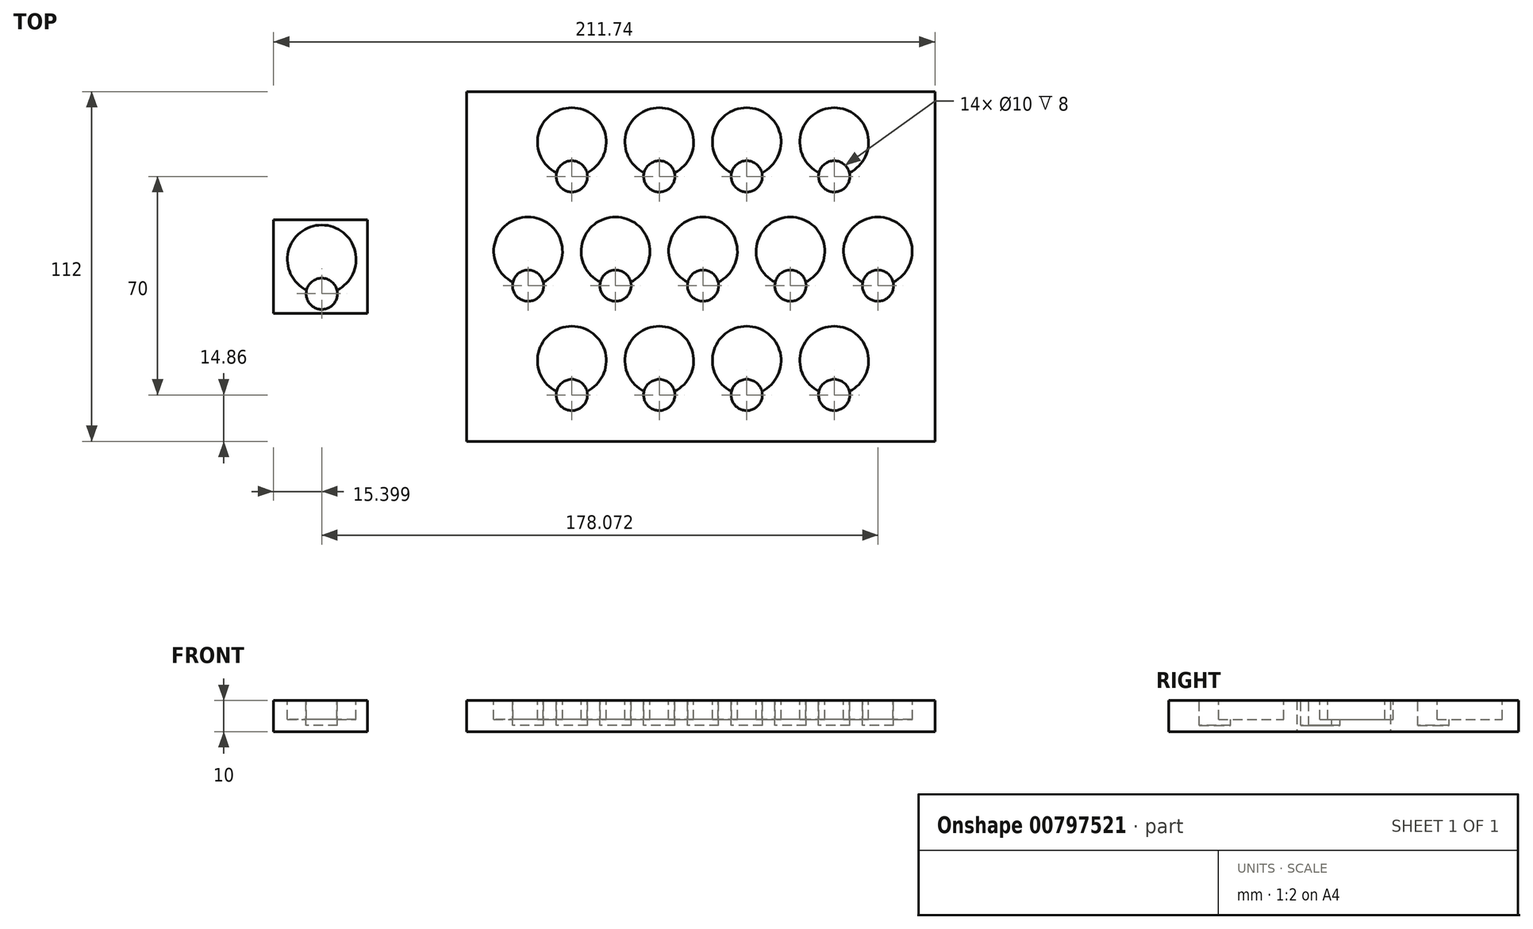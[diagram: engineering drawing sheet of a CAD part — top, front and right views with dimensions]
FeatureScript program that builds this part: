
annotation { "Feature Type Name" : "Feature", "Feature Type Description" : "" }
export const myFeature = defineFeature(function(context is Context, id is Id, definition is map)
    precondition{}
    {
        {
            var Q0;
            Q0=qCreatedBy(makeId("Top.planeOp"),FACE);
            var sketch = newSketch(context, id + "F0", { "sketchPlane" : qUnion([Q0])});
            skLineSegment(sketch, "E0.bottom", {"start": v(-75, 56) * mm, "end": v(75, 56) * mm});
            skLineSegment(sketch, "E0.top", {"start": v(-75, -56) * mm, "end": v(75, -56) * mm});
            skLineSegment(sketch, "E0.left", {"start": v(-75, 56) * mm, "end": v(-75, -56) * mm});
            skLineSegment(sketch, "E0.right", {"start": v(75, 56) * mm, "end": v(75, -56) * mm});
            skPoint(sketch, "E0.middle", {"position": v(0, 0) * mm});
            skLineSegment(sketch, "E1.bottom", {"start": v(-136.74, -15) * mm, "end": v(-106.74, -15) * mm});
            skLineSegment(sketch, "E1.top", {"start": v(-136.74, 15) * mm, "end": v(-106.74, 15) * mm});
            skLineSegment(sketch, "E1.left", {"start": v(-136.74, -15) * mm, "end": v(-136.74, 15) * mm});
            skLineSegment(sketch, "E1.right", {"start": v(-106.74, -15) * mm, "end": v(-106.74, 15) * mm});
            skPoint(sketch, "E1.middle", {"position": v(-121.74, 0) * mm});
            skSolve(sketch);
        }
        {
            var Q0;
            Q0=makeQuery(id+"F0.imprint","IMPRINT",FACE,{"disambiguationData":[TD([[makeQuery(id+"F0.imprint","IMPRINT",EDGE,{"derivedFrom":sQuery(id+"F0.wireOp",EDGE,"E0.bottom")}),-1.0]])]});
            extrude(context, id + "F1", {"entities" : qUnion([Q0]), "depth" : 10 * mm, "offsetDistance" : 25 * mm});
        }
        {
            var Q0;
            Q0=makeQuery(id+"F1.opExtrude","CAP_FACE",FACE,{"disambiguationData":[OSD([sQuery(id+"F0.wireOp",EDGE,"E0.bottom"),sQuery(id+"F0.wireOp",EDGE,"E0.top"),sQuery(id+"F0.wireOp",EDGE,"E0.left"),sQuery(id+"F0.wireOp",EDGE,"E0.right")])],"isStart":false});
            var sketch = newSketch(context, id + "F2", { "sketchPlane" : qUnion([Q0])});
            skCircle(sketch, "E2", {"center": v(-13.27, 39.86) * mm, "radius": 11 * mm});
            skCircle(sketch, "E3", {"center": v(14.73, 39.86) * mm, "radius": 11 * mm});
            skCircle(sketch, "E4", {"center": v(0.73, 4.86) * mm, "radius": 11 * mm});
            skCircle(sketch, "E5", {"center": v(28.73, 4.86) * mm, "radius": 11 * mm});
            skCircle(sketch, "E6", {"center": v(42.73, 39.86) * mm, "radius": 11 * mm});
            skCircle(sketch, "E7", {"center": v(56.73, 4.86) * mm, "radius": 11 * mm});
            skCircle(sketch, "E8", {"center": v(-13.27, -30.14) * mm, "radius": 11 * mm});
            skCircle(sketch, "E9", {"center": v(14.73, -30.14) * mm, "radius": 11 * mm});
            skCircle(sketch, "E10", {"center": v(42.73, -30.14) * mm, "radius": 11 * mm});
            skCircle(sketch, "E11", {"center": v(-27.27, 4.86) * mm, "radius": 11 * mm});
            skCircle(sketch, "E12", {"center": v(-55.27, 4.86) * mm, "radius": 11 * mm});
            skCircle(sketch, "E13", {"center": v(-41.27, 39.86) * mm, "radius": 11 * mm});
            skCircle(sketch, "E14", {"center": v(-41.27, -30.14) * mm, "radius": 11 * mm});
            skLineSegment(sketch, "E15", {"start": v(-41.27, 39.86) * mm, "end": v(-41.27, -30.14) * mm, "construction": true});
            skCircle(sketch, "E16", {"center": v(-13.27, 28.86) * mm, "radius": 5 * mm});
            skCircle(sketch, "E17", {"center": v(14.73, 28.86) * mm, "radius": 5 * mm});
            skCircle(sketch, "E18", {"center": v(42.73, 28.86) * mm, "radius": 5 * mm});
            skCircle(sketch, "E19", {"center": v(-41.27, 28.86) * mm, "radius": 5 * mm});
            skCircle(sketch, "E20", {"center": v(-55.27, -6.14) * mm, "radius": 5 * mm});
            skCircle(sketch, "E21", {"center": v(-27.27, -6.14) * mm, "radius": 5 * mm});
            skCircle(sketch, "E22", {"center": v(0.73, -6.14) * mm, "radius": 5 * mm});
            skCircle(sketch, "E23", {"center": v(28.73, -6.14) * mm, "radius": 5 * mm});
            skCircle(sketch, "E24", {"center": v(56.73, -6.14) * mm, "radius": 5 * mm});
            skCircle(sketch, "E25", {"center": v(-41.27, -41.14) * mm, "radius": 5 * mm});
            skCircle(sketch, "E26", {"center": v(-13.27, -41.14) * mm, "radius": 5 * mm});
            skCircle(sketch, "E27", {"center": v(14.73, -41.14) * mm, "radius": 5 * mm});
            skCircle(sketch, "E28", {"center": v(42.73, -41.14) * mm, "radius": 5 * mm});
            skSolve(sketch);
        }
        {
            var Q0;
            {var subQ0=sQuery(id+"F2.wireOp",EDGE,"E25");var subQ1=sQuery(id+"F2.wireOp",EDGE,"E14");var subQ2=makeQuery(id+"F2.imprint","INTERSECT",VERTEX,{"disambiguationData":[OD(0.0)],"derivedFrom":[subQ1,subQ0]});Q0=makeQuery(id+"F2.imprint","IMPRINT",FACE,{"disambiguationData":[TD([[makeQuery(id+"F2.imprint","IMPRINT",EDGE,{"disambiguationData":[TD([[subQ2,1.0]])],"derivedFrom":subQ1}),1.0]])]});}
            var Q1;
            {var subQ0=sQuery(id+"F2.wireOp",EDGE,"E27");var subQ1=sQuery(id+"F2.wireOp",EDGE,"E9");var subQ2=makeQuery(id+"F2.imprint","INTERSECT",VERTEX,{"disambiguationData":[OD(0.0)],"derivedFrom":[subQ1,subQ0]});Q1=makeQuery(id+"F2.imprint","IMPRINT",FACE,{"disambiguationData":[TD([[makeQuery(id+"F2.imprint","IMPRINT",EDGE,{"disambiguationData":[TD([[subQ2,-1.0]])],"derivedFrom":subQ1}),-1.0]])]});}
            var Q2;
            {var subQ0=sQuery(id+"F2.wireOp",EDGE,"E28");var subQ1=sQuery(id+"F2.wireOp",EDGE,"E10");var subQ2=makeQuery(id+"F2.imprint","INTERSECT",VERTEX,{"disambiguationData":[OD(0.0)],"derivedFrom":[subQ1,subQ0]});Q2=makeQuery(id+"F2.imprint","IMPRINT",FACE,{"disambiguationData":[TD([[makeQuery(id+"F2.imprint","IMPRINT",EDGE,{"disambiguationData":[TD([[subQ2,-1.0]])],"derivedFrom":subQ1}),1.0]])]});}
            var Q3;
            {var subQ0=sQuery(id+"F2.wireOp",EDGE,"E19");var subQ1=sQuery(id+"F2.wireOp",EDGE,"E13");var subQ2=makeQuery(id+"F2.imprint","INTERSECT",VERTEX,{"disambiguationData":[OD(0.0)],"derivedFrom":[subQ1,subQ0]});Q3=makeQuery(id+"F2.imprint","IMPRINT",FACE,{"disambiguationData":[TD([[makeQuery(id+"F2.imprint","IMPRINT",EDGE,{"disambiguationData":[TD([[subQ2,1.0]])],"derivedFrom":subQ1}),1.0]])]});}
            var Q4;
            {var subQ0=sQuery(id+"F2.wireOp",EDGE,"E26");var subQ1=sQuery(id+"F2.wireOp",EDGE,"E8");var subQ2=makeQuery(id+"F2.imprint","INTERSECT",VERTEX,{"disambiguationData":[OD(0.0)],"derivedFrom":[subQ1,subQ0]});Q4=makeQuery(id+"F2.imprint","IMPRINT",FACE,{"disambiguationData":[TD([[makeQuery(id+"F2.imprint","IMPRINT",EDGE,{"disambiguationData":[TD([[subQ2,-1.0]])],"derivedFrom":subQ1}),-1.0]])]});}
            var Q5;
            {var subQ0=sQuery(id+"F2.wireOp",EDGE,"E21");var subQ1=sQuery(id+"F2.wireOp",EDGE,"E11");var subQ2=makeQuery(id+"F2.imprint","INTERSECT",VERTEX,{"disambiguationData":[OD(0.0)],"derivedFrom":[subQ1,subQ0]});Q5=makeQuery(id+"F2.imprint","IMPRINT",FACE,{"disambiguationData":[TD([[makeQuery(id+"F2.imprint","IMPRINT",EDGE,{"disambiguationData":[TD([[subQ2,-1.0]])],"derivedFrom":subQ1}),-1.0]])]});}
            var Q6;
            {var subQ0=sQuery(id+"F2.wireOp",EDGE,"E18");var subQ1=sQuery(id+"F2.wireOp",EDGE,"E6");var subQ2=makeQuery(id+"F2.imprint","INTERSECT",VERTEX,{"disambiguationData":[OD(0.0)],"derivedFrom":[subQ1,subQ0]});Q6=makeQuery(id+"F2.imprint","IMPRINT",FACE,{"disambiguationData":[TD([[makeQuery(id+"F2.imprint","IMPRINT",EDGE,{"disambiguationData":[TD([[subQ2,-1.0]])],"derivedFrom":subQ1}),1.0]])]});}
            var Q7;
            {var subQ0=sQuery(id+"F2.wireOp",EDGE,"E28");var subQ1=sQuery(id+"F2.wireOp",EDGE,"E10");var subQ2=makeQuery(id+"F2.imprint","INTERSECT",VERTEX,{"disambiguationData":[OD(0.0)],"derivedFrom":[subQ1,subQ0]});Q7=makeQuery(id+"F2.imprint","IMPRINT",FACE,{"disambiguationData":[TD([[makeQuery(id+"F2.imprint","IMPRINT",EDGE,{"disambiguationData":[TD([[subQ2,-1.0]])],"derivedFrom":subQ1}),-1.0]])]});}
            var Q8;
            {var subQ0=sQuery(id+"F2.wireOp",EDGE,"E24");var subQ1=sQuery(id+"F2.wireOp",EDGE,"E7");var subQ2=makeQuery(id+"F2.imprint","INTERSECT",VERTEX,{"disambiguationData":[OD(0.0)],"derivedFrom":[subQ1,subQ0]});Q8=makeQuery(id+"F2.imprint","IMPRINT",FACE,{"disambiguationData":[TD([[makeQuery(id+"F2.imprint","IMPRINT",EDGE,{"disambiguationData":[TD([[subQ2,1.0]])],"derivedFrom":subQ1}),1.0]])]});}
            var Q9;
            {var subQ0=sQuery(id+"F2.wireOp",EDGE,"E19");var subQ1=sQuery(id+"F2.wireOp",EDGE,"E13");var subQ2=makeQuery(id+"F2.imprint","INTERSECT",VERTEX,{"disambiguationData":[OD(0.0)],"derivedFrom":[subQ1,subQ0]});Q9=makeQuery(id+"F2.imprint","IMPRINT",FACE,{"disambiguationData":[TD([[makeQuery(id+"F2.imprint","IMPRINT",EDGE,{"disambiguationData":[TD([[subQ2,-1.0]])],"derivedFrom":subQ1}),1.0]])]});}
            var Q10;
            {var subQ0=sQuery(id+"F2.wireOp",EDGE,"E24");var subQ1=sQuery(id+"F2.wireOp",EDGE,"E7");var subQ2=makeQuery(id+"F2.imprint","INTERSECT",VERTEX,{"disambiguationData":[OD(0.0)],"derivedFrom":[subQ1,subQ0]});Q10=makeQuery(id+"F2.imprint","IMPRINT",FACE,{"disambiguationData":[TD([[makeQuery(id+"F2.imprint","IMPRINT",EDGE,{"disambiguationData":[TD([[subQ2,-1.0]])],"derivedFrom":subQ1}),1.0]])]});}
            var Q11;
            {var subQ0=sQuery(id+"F2.wireOp",EDGE,"E27");var subQ1=sQuery(id+"F2.wireOp",EDGE,"E9");var subQ2=makeQuery(id+"F2.imprint","INTERSECT",VERTEX,{"disambiguationData":[OD(0.0)],"derivedFrom":[subQ1,subQ0]});Q11=makeQuery(id+"F2.imprint","IMPRINT",FACE,{"disambiguationData":[TD([[makeQuery(id+"F2.imprint","IMPRINT",EDGE,{"disambiguationData":[TD([[subQ2,-1.0]])],"derivedFrom":subQ1}),1.0]])]});}
            var Q12;
            {var subQ0=sQuery(id+"F2.wireOp",EDGE,"E25");var subQ1=sQuery(id+"F2.wireOp",EDGE,"E14");var subQ2=makeQuery(id+"F2.imprint","INTERSECT",VERTEX,{"disambiguationData":[OD(0.0)],"derivedFrom":[subQ1,subQ0]});Q12=makeQuery(id+"F2.imprint","IMPRINT",FACE,{"disambiguationData":[TD([[makeQuery(id+"F2.imprint","IMPRINT",EDGE,{"disambiguationData":[TD([[subQ2,-1.0]])],"derivedFrom":subQ1}),-1.0]])]});}
            var Q13;
            {var subQ0=sQuery(id+"F2.wireOp",EDGE,"E23");var subQ1=sQuery(id+"F2.wireOp",EDGE,"E5");var subQ2=makeQuery(id+"F2.imprint","INTERSECT",VERTEX,{"disambiguationData":[OD(0.0)],"derivedFrom":[subQ1,subQ0]});Q13=makeQuery(id+"F2.imprint","IMPRINT",FACE,{"disambiguationData":[TD([[makeQuery(id+"F2.imprint","IMPRINT",EDGE,{"disambiguationData":[TD([[subQ2,1.0]])],"derivedFrom":subQ1}),1.0]])]});}
            var Q14;
            {var subQ0=sQuery(id+"F2.wireOp",EDGE,"E26");var subQ1=sQuery(id+"F2.wireOp",EDGE,"E8");var subQ2=makeQuery(id+"F2.imprint","INTERSECT",VERTEX,{"disambiguationData":[OD(0.0)],"derivedFrom":[subQ1,subQ0]});Q14=makeQuery(id+"F2.imprint","IMPRINT",FACE,{"disambiguationData":[TD([[makeQuery(id+"F2.imprint","IMPRINT",EDGE,{"disambiguationData":[TD([[subQ2,-1.0]])],"derivedFrom":subQ1}),1.0]])]});}
            var Q15;
            {var subQ0=sQuery(id+"F2.wireOp",EDGE,"E22");var subQ1=sQuery(id+"F2.wireOp",EDGE,"E4");var subQ2=makeQuery(id+"F2.imprint","INTERSECT",VERTEX,{"disambiguationData":[OD(0.0)],"derivedFrom":[subQ1,subQ0]});Q15=makeQuery(id+"F2.imprint","IMPRINT",FACE,{"disambiguationData":[TD([[makeQuery(id+"F2.imprint","IMPRINT",EDGE,{"disambiguationData":[TD([[subQ2,-1.0]])],"derivedFrom":subQ1}),-1.0]])]});}
            var Q16;
            {var subQ0=sQuery(id+"F2.wireOp",EDGE,"E20");var subQ1=sQuery(id+"F2.wireOp",EDGE,"E12");var subQ2=makeQuery(id+"F2.imprint","INTERSECT",VERTEX,{"disambiguationData":[OD(0.0)],"derivedFrom":[subQ1,subQ0]});Q16=makeQuery(id+"F2.imprint","IMPRINT",FACE,{"disambiguationData":[TD([[makeQuery(id+"F2.imprint","IMPRINT",EDGE,{"disambiguationData":[TD([[subQ2,-1.0]])],"derivedFrom":subQ1}),-1.0]])]});}
            var Q17;
            {var subQ0=sQuery(id+"F2.wireOp",EDGE,"E19");var subQ1=sQuery(id+"F2.wireOp",EDGE,"E13");var subQ2=makeQuery(id+"F2.imprint","INTERSECT",VERTEX,{"disambiguationData":[OD(0.0)],"derivedFrom":[subQ1,subQ0]});Q17=makeQuery(id+"F2.imprint","IMPRINT",FACE,{"disambiguationData":[TD([[makeQuery(id+"F2.imprint","IMPRINT",EDGE,{"disambiguationData":[TD([[subQ2,-1.0]])],"derivedFrom":subQ1}),-1.0]])]});}
            var Q18;
            {var subQ0=sQuery(id+"F2.wireOp",EDGE,"E17");var subQ1=sQuery(id+"F2.wireOp",EDGE,"E3");var subQ2=makeQuery(id+"F2.imprint","INTERSECT",VERTEX,{"disambiguationData":[OD(0.0)],"derivedFrom":[subQ1,subQ0]});Q18=makeQuery(id+"F2.imprint","IMPRINT",FACE,{"disambiguationData":[TD([[makeQuery(id+"F2.imprint","IMPRINT",EDGE,{"disambiguationData":[TD([[subQ2,-1.0]])],"derivedFrom":subQ1}),-1.0]])]});}
            var Q19;
            {var subQ0=sQuery(id+"F2.wireOp",EDGE,"E17");var subQ1=sQuery(id+"F2.wireOp",EDGE,"E3");var subQ2=makeQuery(id+"F2.imprint","INTERSECT",VERTEX,{"disambiguationData":[OD(0.0)],"derivedFrom":[subQ1,subQ0]});Q19=makeQuery(id+"F2.imprint","IMPRINT",FACE,{"disambiguationData":[TD([[makeQuery(id+"F2.imprint","IMPRINT",EDGE,{"disambiguationData":[TD([[subQ2,-1.0]])],"derivedFrom":subQ1}),1.0]])]});}
            var Q20;
            {var subQ0=sQuery(id+"F2.wireOp",EDGE,"E22");var subQ1=sQuery(id+"F2.wireOp",EDGE,"E4");var subQ2=makeQuery(id+"F2.imprint","INTERSECT",VERTEX,{"disambiguationData":[OD(0.0)],"derivedFrom":[subQ1,subQ0]});Q20=makeQuery(id+"F2.imprint","IMPRINT",FACE,{"disambiguationData":[TD([[makeQuery(id+"F2.imprint","IMPRINT",EDGE,{"disambiguationData":[TD([[subQ2,1.0]])],"derivedFrom":subQ1}),1.0]])]});}
            var Q21;
            {var subQ0=sQuery(id+"F2.wireOp",EDGE,"E20");var subQ1=sQuery(id+"F2.wireOp",EDGE,"E12");var subQ2=makeQuery(id+"F2.imprint","INTERSECT",VERTEX,{"disambiguationData":[OD(0.0)],"derivedFrom":[subQ1,subQ0]});Q21=makeQuery(id+"F2.imprint","IMPRINT",FACE,{"disambiguationData":[TD([[makeQuery(id+"F2.imprint","IMPRINT",EDGE,{"disambiguationData":[TD([[subQ2,-1.0]])],"derivedFrom":subQ1}),1.0]])]});}
            var Q22;
            {var subQ0=sQuery(id+"F2.wireOp",EDGE,"E23");var subQ1=sQuery(id+"F2.wireOp",EDGE,"E5");var subQ2=makeQuery(id+"F2.imprint","INTERSECT",VERTEX,{"disambiguationData":[OD(0.0)],"derivedFrom":[subQ1,subQ0]});Q22=makeQuery(id+"F2.imprint","IMPRINT",FACE,{"disambiguationData":[TD([[makeQuery(id+"F2.imprint","IMPRINT",EDGE,{"disambiguationData":[TD([[subQ2,-1.0]])],"derivedFrom":subQ1}),-1.0]])]});}
            var Q23;
            {var subQ0=sQuery(id+"F2.wireOp",EDGE,"E23");var subQ1=sQuery(id+"F2.wireOp",EDGE,"E5");var subQ2=makeQuery(id+"F2.imprint","INTERSECT",VERTEX,{"disambiguationData":[OD(0.0)],"derivedFrom":[subQ1,subQ0]});Q23=makeQuery(id+"F2.imprint","IMPRINT",FACE,{"disambiguationData":[TD([[makeQuery(id+"F2.imprint","IMPRINT",EDGE,{"disambiguationData":[TD([[subQ2,-1.0]])],"derivedFrom":subQ1}),1.0]])]});}
            var Q24;
            {var subQ0=sQuery(id+"F2.wireOp",EDGE,"E17");var subQ1=sQuery(id+"F2.wireOp",EDGE,"E3");var subQ2=makeQuery(id+"F2.imprint","INTERSECT",VERTEX,{"disambiguationData":[OD(0.0)],"derivedFrom":[subQ1,subQ0]});Q24=makeQuery(id+"F2.imprint","IMPRINT",FACE,{"disambiguationData":[TD([[makeQuery(id+"F2.imprint","IMPRINT",EDGE,{"disambiguationData":[TD([[subQ2,1.0]])],"derivedFrom":subQ1}),1.0]])]});}
            var Q25;
            {var subQ0=sQuery(id+"F2.wireOp",EDGE,"E16");var subQ1=sQuery(id+"F2.wireOp",EDGE,"E2");var subQ2=makeQuery(id+"F2.imprint","INTERSECT",VERTEX,{"disambiguationData":[OD(0.0)],"derivedFrom":[subQ1,subQ0]});Q25=makeQuery(id+"F2.imprint","IMPRINT",FACE,{"disambiguationData":[TD([[makeQuery(id+"F2.imprint","IMPRINT",EDGE,{"disambiguationData":[TD([[subQ2,1.0]])],"derivedFrom":subQ1}),1.0]])]});}
            var Q26;
            {var subQ0=sQuery(id+"F2.wireOp",EDGE,"E18");var subQ1=sQuery(id+"F2.wireOp",EDGE,"E6");var subQ2=makeQuery(id+"F2.imprint","INTERSECT",VERTEX,{"disambiguationData":[OD(0.0)],"derivedFrom":[subQ1,subQ0]});Q26=makeQuery(id+"F2.imprint","IMPRINT",FACE,{"disambiguationData":[TD([[makeQuery(id+"F2.imprint","IMPRINT",EDGE,{"disambiguationData":[TD([[subQ2,-1.0]])],"derivedFrom":subQ1}),-1.0]])]});}
            var Q27;
            {var subQ0=sQuery(id+"F2.wireOp",EDGE,"E16");var subQ1=sQuery(id+"F2.wireOp",EDGE,"E2");var subQ2=makeQuery(id+"F2.imprint","INTERSECT",VERTEX,{"disambiguationData":[OD(0.0)],"derivedFrom":[subQ1,subQ0]});Q27=makeQuery(id+"F2.imprint","IMPRINT",FACE,{"disambiguationData":[TD([[makeQuery(id+"F2.imprint","IMPRINT",EDGE,{"disambiguationData":[TD([[subQ2,-1.0]])],"derivedFrom":subQ1}),-1.0]])]});}
            var Q28;
            {var subQ0=sQuery(id+"F2.wireOp",EDGE,"E16");var subQ1=sQuery(id+"F2.wireOp",EDGE,"E2");var subQ2=makeQuery(id+"F2.imprint","INTERSECT",VERTEX,{"disambiguationData":[OD(0.0)],"derivedFrom":[subQ1,subQ0]});Q28=makeQuery(id+"F2.imprint","IMPRINT",FACE,{"disambiguationData":[TD([[makeQuery(id+"F2.imprint","IMPRINT",EDGE,{"disambiguationData":[TD([[subQ2,-1.0]])],"derivedFrom":subQ1}),1.0]])]});}
            var Q29;
            {var subQ0=sQuery(id+"F2.wireOp",EDGE,"E18");var subQ1=sQuery(id+"F2.wireOp",EDGE,"E6");var subQ2=makeQuery(id+"F2.imprint","INTERSECT",VERTEX,{"disambiguationData":[OD(0.0)],"derivedFrom":[subQ1,subQ0]});Q29=makeQuery(id+"F2.imprint","IMPRINT",FACE,{"disambiguationData":[TD([[makeQuery(id+"F2.imprint","IMPRINT",EDGE,{"disambiguationData":[TD([[subQ2,1.0]])],"derivedFrom":subQ1}),1.0]])]});}
            var Q30;
            {var subQ0=sQuery(id+"F2.wireOp",EDGE,"E27");var subQ1=sQuery(id+"F2.wireOp",EDGE,"E9");var subQ2=makeQuery(id+"F2.imprint","INTERSECT",VERTEX,{"disambiguationData":[OD(0.0)],"derivedFrom":[subQ1,subQ0]});Q30=makeQuery(id+"F2.imprint","IMPRINT",FACE,{"disambiguationData":[TD([[makeQuery(id+"F2.imprint","IMPRINT",EDGE,{"disambiguationData":[TD([[subQ2,1.0]])],"derivedFrom":subQ1}),1.0]])]});}
            var Q31;
            {var subQ0=sQuery(id+"F2.wireOp",EDGE,"E28");var subQ1=sQuery(id+"F2.wireOp",EDGE,"E10");var subQ2=makeQuery(id+"F2.imprint","INTERSECT",VERTEX,{"disambiguationData":[OD(0.0)],"derivedFrom":[subQ1,subQ0]});Q31=makeQuery(id+"F2.imprint","IMPRINT",FACE,{"disambiguationData":[TD([[makeQuery(id+"F2.imprint","IMPRINT",EDGE,{"disambiguationData":[TD([[subQ2,1.0]])],"derivedFrom":subQ1}),1.0]])]});}
            var Q32;
            {var subQ0=sQuery(id+"F2.wireOp",EDGE,"E21");var subQ1=sQuery(id+"F2.wireOp",EDGE,"E11");var subQ2=makeQuery(id+"F2.imprint","INTERSECT",VERTEX,{"disambiguationData":[OD(0.0)],"derivedFrom":[subQ1,subQ0]});Q32=makeQuery(id+"F2.imprint","IMPRINT",FACE,{"disambiguationData":[TD([[makeQuery(id+"F2.imprint","IMPRINT",EDGE,{"disambiguationData":[TD([[subQ2,1.0]])],"derivedFrom":subQ1}),1.0]])]});}
            var Q33;
            {var subQ0=sQuery(id+"F2.wireOp",EDGE,"E25");var subQ1=sQuery(id+"F2.wireOp",EDGE,"E14");var subQ2=makeQuery(id+"F2.imprint","INTERSECT",VERTEX,{"disambiguationData":[OD(0.0)],"derivedFrom":[subQ1,subQ0]});Q33=makeQuery(id+"F2.imprint","IMPRINT",FACE,{"disambiguationData":[TD([[makeQuery(id+"F2.imprint","IMPRINT",EDGE,{"disambiguationData":[TD([[subQ2,-1.0]])],"derivedFrom":subQ1}),1.0]])]});}
            var Q34;
            {var subQ0=sQuery(id+"F2.wireOp",EDGE,"E21");var subQ1=sQuery(id+"F2.wireOp",EDGE,"E11");var subQ2=makeQuery(id+"F2.imprint","INTERSECT",VERTEX,{"disambiguationData":[OD(0.0)],"derivedFrom":[subQ1,subQ0]});Q34=makeQuery(id+"F2.imprint","IMPRINT",FACE,{"disambiguationData":[TD([[makeQuery(id+"F2.imprint","IMPRINT",EDGE,{"disambiguationData":[TD([[subQ2,-1.0]])],"derivedFrom":subQ1}),1.0]])]});}
            var Q35;
            {var subQ0=sQuery(id+"F2.wireOp",EDGE,"E26");var subQ1=sQuery(id+"F2.wireOp",EDGE,"E8");var subQ2=makeQuery(id+"F2.imprint","INTERSECT",VERTEX,{"disambiguationData":[OD(0.0)],"derivedFrom":[subQ1,subQ0]});Q35=makeQuery(id+"F2.imprint","IMPRINT",FACE,{"disambiguationData":[TD([[makeQuery(id+"F2.imprint","IMPRINT",EDGE,{"disambiguationData":[TD([[subQ2,1.0]])],"derivedFrom":subQ1}),1.0]])]});}
            var Q36;
            {var subQ0=sQuery(id+"F2.wireOp",EDGE,"E20");var subQ1=sQuery(id+"F2.wireOp",EDGE,"E12");var subQ2=makeQuery(id+"F2.imprint","INTERSECT",VERTEX,{"disambiguationData":[OD(0.0)],"derivedFrom":[subQ1,subQ0]});Q36=makeQuery(id+"F2.imprint","IMPRINT",FACE,{"disambiguationData":[TD([[makeQuery(id+"F2.imprint","IMPRINT",EDGE,{"disambiguationData":[TD([[subQ2,1.0]])],"derivedFrom":subQ1}),1.0]])]});}
            var Q37;
            {var subQ0=sQuery(id+"F2.wireOp",EDGE,"E24");var subQ1=sQuery(id+"F2.wireOp",EDGE,"E7");var subQ2=makeQuery(id+"F2.imprint","INTERSECT",VERTEX,{"disambiguationData":[OD(0.0)],"derivedFrom":[subQ1,subQ0]});Q37=makeQuery(id+"F2.imprint","IMPRINT",FACE,{"disambiguationData":[TD([[makeQuery(id+"F2.imprint","IMPRINT",EDGE,{"disambiguationData":[TD([[subQ2,-1.0]])],"derivedFrom":subQ1}),-1.0]])]});}
            var Q38;
            {var subQ0=sQuery(id+"F2.wireOp",EDGE,"E22");var subQ1=sQuery(id+"F2.wireOp",EDGE,"E4");var subQ2=makeQuery(id+"F2.imprint","INTERSECT",VERTEX,{"disambiguationData":[OD(0.0)],"derivedFrom":[subQ1,subQ0]});Q38=makeQuery(id+"F2.imprint","IMPRINT",FACE,{"disambiguationData":[TD([[makeQuery(id+"F2.imprint","IMPRINT",EDGE,{"disambiguationData":[TD([[subQ2,-1.0]])],"derivedFrom":subQ1}),1.0]])]});}
            extrude(context, id + "F3", {"entities" : qUnion([Q0, Q1, Q2, Q3, Q4, Q5, Q6, Q7, Q8, Q9, Q10, Q11, Q12, Q13, Q14, Q15, Q16, Q17, Q18, Q19, Q20, Q21, Q22, Q23, Q24, Q25, Q26, Q27, Q28, Q29, Q30, Q31, Q32, Q33, Q34, Q35, Q36, Q37, Q38]), "operationType" : NewBodyOperationType.REMOVE, "oppositeDirection" : true, "depth" : 6 * mm, "offsetDistance" : 25 * mm});
        }
        {
            var Q0;
            {var subQ0=sQuery(id+"F2.wireOp",EDGE,"E19");var subQ1=sQuery(id+"F2.wireOp",EDGE,"E13");var subQ2=makeQuery(id+"F2.imprint","INTERSECT",VERTEX,{"disambiguationData":[OD(0.0)],"derivedFrom":[subQ1,subQ0]});Q0=makeQuery(id+"F2.imprint","IMPRINT",FACE,{"disambiguationData":[TD([[makeQuery(id+"F2.imprint","IMPRINT",EDGE,{"disambiguationData":[TD([[subQ2,-1.0]])],"derivedFrom":subQ1}),1.0]])]});}
            var Q1;
            {var subQ0=sQuery(id+"F2.wireOp",EDGE,"E19");var subQ1=sQuery(id+"F2.wireOp",EDGE,"E13");var subQ2=makeQuery(id+"F2.imprint","INTERSECT",VERTEX,{"disambiguationData":[OD(0.0)],"derivedFrom":[subQ1,subQ0]});Q1=makeQuery(id+"F2.imprint","IMPRINT",FACE,{"disambiguationData":[TD([[makeQuery(id+"F2.imprint","IMPRINT",EDGE,{"disambiguationData":[TD([[subQ2,-1.0]])],"derivedFrom":subQ1}),-1.0]])]});}
            var Q2;
            {var subQ0=sQuery(id+"F2.wireOp",EDGE,"E16");var subQ1=sQuery(id+"F2.wireOp",EDGE,"E2");var subQ2=makeQuery(id+"F2.imprint","INTERSECT",VERTEX,{"disambiguationData":[OD(0.0)],"derivedFrom":[subQ1,subQ0]});Q2=makeQuery(id+"F2.imprint","IMPRINT",FACE,{"disambiguationData":[TD([[makeQuery(id+"F2.imprint","IMPRINT",EDGE,{"disambiguationData":[TD([[subQ2,-1.0]])],"derivedFrom":subQ1}),1.0]])]});}
            var Q3;
            {var subQ0=sQuery(id+"F2.wireOp",EDGE,"E16");var subQ1=sQuery(id+"F2.wireOp",EDGE,"E2");var subQ2=makeQuery(id+"F2.imprint","INTERSECT",VERTEX,{"disambiguationData":[OD(0.0)],"derivedFrom":[subQ1,subQ0]});Q3=makeQuery(id+"F2.imprint","IMPRINT",FACE,{"disambiguationData":[TD([[makeQuery(id+"F2.imprint","IMPRINT",EDGE,{"disambiguationData":[TD([[subQ2,-1.0]])],"derivedFrom":subQ1}),-1.0]])]});}
            var Q4;
            {var subQ0=sQuery(id+"F2.wireOp",EDGE,"E17");var subQ1=sQuery(id+"F2.wireOp",EDGE,"E3");var subQ2=makeQuery(id+"F2.imprint","INTERSECT",VERTEX,{"disambiguationData":[OD(0.0)],"derivedFrom":[subQ1,subQ0]});Q4=makeQuery(id+"F2.imprint","IMPRINT",FACE,{"disambiguationData":[TD([[makeQuery(id+"F2.imprint","IMPRINT",EDGE,{"disambiguationData":[TD([[subQ2,-1.0]])],"derivedFrom":subQ1}),1.0]])]});}
            var Q5;
            {var subQ0=sQuery(id+"F2.wireOp",EDGE,"E17");var subQ1=sQuery(id+"F2.wireOp",EDGE,"E3");var subQ2=makeQuery(id+"F2.imprint","INTERSECT",VERTEX,{"disambiguationData":[OD(0.0)],"derivedFrom":[subQ1,subQ0]});Q5=makeQuery(id+"F2.imprint","IMPRINT",FACE,{"disambiguationData":[TD([[makeQuery(id+"F2.imprint","IMPRINT",EDGE,{"disambiguationData":[TD([[subQ2,-1.0]])],"derivedFrom":subQ1}),-1.0]])]});}
            var Q6;
            {var subQ0=sQuery(id+"F2.wireOp",EDGE,"E18");var subQ1=sQuery(id+"F2.wireOp",EDGE,"E6");var subQ2=makeQuery(id+"F2.imprint","INTERSECT",VERTEX,{"disambiguationData":[OD(0.0)],"derivedFrom":[subQ1,subQ0]});Q6=makeQuery(id+"F2.imprint","IMPRINT",FACE,{"disambiguationData":[TD([[makeQuery(id+"F2.imprint","IMPRINT",EDGE,{"disambiguationData":[TD([[subQ2,-1.0]])],"derivedFrom":subQ1}),1.0]])]});}
            var Q7;
            {var subQ0=sQuery(id+"F2.wireOp",EDGE,"E18");var subQ1=sQuery(id+"F2.wireOp",EDGE,"E6");var subQ2=makeQuery(id+"F2.imprint","INTERSECT",VERTEX,{"disambiguationData":[OD(0.0)],"derivedFrom":[subQ1,subQ0]});Q7=makeQuery(id+"F2.imprint","IMPRINT",FACE,{"disambiguationData":[TD([[makeQuery(id+"F2.imprint","IMPRINT",EDGE,{"disambiguationData":[TD([[subQ2,-1.0]])],"derivedFrom":subQ1}),-1.0]])]});}
            var Q8;
            {var subQ0=sQuery(id+"F2.wireOp",EDGE,"E20");var subQ1=sQuery(id+"F2.wireOp",EDGE,"E12");var subQ2=makeQuery(id+"F2.imprint","INTERSECT",VERTEX,{"disambiguationData":[OD(0.0)],"derivedFrom":[subQ1,subQ0]});Q8=makeQuery(id+"F2.imprint","IMPRINT",FACE,{"disambiguationData":[TD([[makeQuery(id+"F2.imprint","IMPRINT",EDGE,{"disambiguationData":[TD([[subQ2,-1.0]])],"derivedFrom":subQ1}),1.0]])]});}
            var Q9;
            {var subQ0=sQuery(id+"F2.wireOp",EDGE,"E20");var subQ1=sQuery(id+"F2.wireOp",EDGE,"E12");var subQ2=makeQuery(id+"F2.imprint","INTERSECT",VERTEX,{"disambiguationData":[OD(0.0)],"derivedFrom":[subQ1,subQ0]});Q9=makeQuery(id+"F2.imprint","IMPRINT",FACE,{"disambiguationData":[TD([[makeQuery(id+"F2.imprint","IMPRINT",EDGE,{"disambiguationData":[TD([[subQ2,-1.0]])],"derivedFrom":subQ1}),-1.0]])]});}
            var Q10;
            {var subQ0=sQuery(id+"F2.wireOp",EDGE,"E21");var subQ1=sQuery(id+"F2.wireOp",EDGE,"E11");var subQ2=makeQuery(id+"F2.imprint","INTERSECT",VERTEX,{"disambiguationData":[OD(0.0)],"derivedFrom":[subQ1,subQ0]});Q10=makeQuery(id+"F2.imprint","IMPRINT",FACE,{"disambiguationData":[TD([[makeQuery(id+"F2.imprint","IMPRINT",EDGE,{"disambiguationData":[TD([[subQ2,-1.0]])],"derivedFrom":subQ1}),1.0]])]});}
            var Q11;
            {var subQ0=sQuery(id+"F2.wireOp",EDGE,"E21");var subQ1=sQuery(id+"F2.wireOp",EDGE,"E11");var subQ2=makeQuery(id+"F2.imprint","INTERSECT",VERTEX,{"disambiguationData":[OD(0.0)],"derivedFrom":[subQ1,subQ0]});Q11=makeQuery(id+"F2.imprint","IMPRINT",FACE,{"disambiguationData":[TD([[makeQuery(id+"F2.imprint","IMPRINT",EDGE,{"disambiguationData":[TD([[subQ2,-1.0]])],"derivedFrom":subQ1}),-1.0]])]});}
            var Q12;
            {var subQ0=sQuery(id+"F2.wireOp",EDGE,"E22");var subQ1=sQuery(id+"F2.wireOp",EDGE,"E4");var subQ2=makeQuery(id+"F2.imprint","INTERSECT",VERTEX,{"disambiguationData":[OD(0.0)],"derivedFrom":[subQ1,subQ0]});Q12=makeQuery(id+"F2.imprint","IMPRINT",FACE,{"disambiguationData":[TD([[makeQuery(id+"F2.imprint","IMPRINT",EDGE,{"disambiguationData":[TD([[subQ2,-1.0]])],"derivedFrom":subQ1}),1.0]])]});}
            var Q13;
            {var subQ0=sQuery(id+"F2.wireOp",EDGE,"E22");var subQ1=sQuery(id+"F2.wireOp",EDGE,"E4");var subQ2=makeQuery(id+"F2.imprint","INTERSECT",VERTEX,{"disambiguationData":[OD(0.0)],"derivedFrom":[subQ1,subQ0]});Q13=makeQuery(id+"F2.imprint","IMPRINT",FACE,{"disambiguationData":[TD([[makeQuery(id+"F2.imprint","IMPRINT",EDGE,{"disambiguationData":[TD([[subQ2,-1.0]])],"derivedFrom":subQ1}),-1.0]])]});}
            var Q14;
            {var subQ0=sQuery(id+"F2.wireOp",EDGE,"E23");var subQ1=sQuery(id+"F2.wireOp",EDGE,"E5");var subQ2=makeQuery(id+"F2.imprint","INTERSECT",VERTEX,{"disambiguationData":[OD(0.0)],"derivedFrom":[subQ1,subQ0]});Q14=makeQuery(id+"F2.imprint","IMPRINT",FACE,{"disambiguationData":[TD([[makeQuery(id+"F2.imprint","IMPRINT",EDGE,{"disambiguationData":[TD([[subQ2,-1.0]])],"derivedFrom":subQ1}),1.0]])]});}
            var Q15;
            {var subQ0=sQuery(id+"F2.wireOp",EDGE,"E23");var subQ1=sQuery(id+"F2.wireOp",EDGE,"E5");var subQ2=makeQuery(id+"F2.imprint","INTERSECT",VERTEX,{"disambiguationData":[OD(0.0)],"derivedFrom":[subQ1,subQ0]});Q15=makeQuery(id+"F2.imprint","IMPRINT",FACE,{"disambiguationData":[TD([[makeQuery(id+"F2.imprint","IMPRINT",EDGE,{"disambiguationData":[TD([[subQ2,-1.0]])],"derivedFrom":subQ1}),-1.0]])]});}
            var Q16;
            {var subQ0=sQuery(id+"F2.wireOp",EDGE,"E24");var subQ1=sQuery(id+"F2.wireOp",EDGE,"E7");var subQ2=makeQuery(id+"F2.imprint","INTERSECT",VERTEX,{"disambiguationData":[OD(0.0)],"derivedFrom":[subQ1,subQ0]});Q16=makeQuery(id+"F2.imprint","IMPRINT",FACE,{"disambiguationData":[TD([[makeQuery(id+"F2.imprint","IMPRINT",EDGE,{"disambiguationData":[TD([[subQ2,-1.0]])],"derivedFrom":subQ1}),1.0]])]});}
            var Q17;
            {var subQ0=sQuery(id+"F2.wireOp",EDGE,"E24");var subQ1=sQuery(id+"F2.wireOp",EDGE,"E7");var subQ2=makeQuery(id+"F2.imprint","INTERSECT",VERTEX,{"disambiguationData":[OD(0.0)],"derivedFrom":[subQ1,subQ0]});Q17=makeQuery(id+"F2.imprint","IMPRINT",FACE,{"disambiguationData":[TD([[makeQuery(id+"F2.imprint","IMPRINT",EDGE,{"disambiguationData":[TD([[subQ2,-1.0]])],"derivedFrom":subQ1}),-1.0]])]});}
            var Q18;
            {var subQ0=sQuery(id+"F2.wireOp",EDGE,"E25");var subQ1=sQuery(id+"F2.wireOp",EDGE,"E14");var subQ2=makeQuery(id+"F2.imprint","INTERSECT",VERTEX,{"disambiguationData":[OD(0.0)],"derivedFrom":[subQ1,subQ0]});Q18=makeQuery(id+"F2.imprint","IMPRINT",FACE,{"disambiguationData":[TD([[makeQuery(id+"F2.imprint","IMPRINT",EDGE,{"disambiguationData":[TD([[subQ2,-1.0]])],"derivedFrom":subQ1}),1.0]])]});}
            var Q19;
            {var subQ0=sQuery(id+"F2.wireOp",EDGE,"E25");var subQ1=sQuery(id+"F2.wireOp",EDGE,"E14");var subQ2=makeQuery(id+"F2.imprint","INTERSECT",VERTEX,{"disambiguationData":[OD(0.0)],"derivedFrom":[subQ1,subQ0]});Q19=makeQuery(id+"F2.imprint","IMPRINT",FACE,{"disambiguationData":[TD([[makeQuery(id+"F2.imprint","IMPRINT",EDGE,{"disambiguationData":[TD([[subQ2,-1.0]])],"derivedFrom":subQ1}),-1.0]])]});}
            var Q20;
            {var subQ0=sQuery(id+"F2.wireOp",EDGE,"E26");var subQ1=sQuery(id+"F2.wireOp",EDGE,"E8");var subQ2=makeQuery(id+"F2.imprint","INTERSECT",VERTEX,{"disambiguationData":[OD(0.0)],"derivedFrom":[subQ1,subQ0]});Q20=makeQuery(id+"F2.imprint","IMPRINT",FACE,{"disambiguationData":[TD([[makeQuery(id+"F2.imprint","IMPRINT",EDGE,{"disambiguationData":[TD([[subQ2,-1.0]])],"derivedFrom":subQ1}),1.0]])]});}
            var Q21;
            {var subQ0=sQuery(id+"F2.wireOp",EDGE,"E26");var subQ1=sQuery(id+"F2.wireOp",EDGE,"E8");var subQ2=makeQuery(id+"F2.imprint","INTERSECT",VERTEX,{"disambiguationData":[OD(0.0)],"derivedFrom":[subQ1,subQ0]});Q21=makeQuery(id+"F2.imprint","IMPRINT",FACE,{"disambiguationData":[TD([[makeQuery(id+"F2.imprint","IMPRINT",EDGE,{"disambiguationData":[TD([[subQ2,-1.0]])],"derivedFrom":subQ1}),-1.0]])]});}
            var Q22;
            {var subQ0=sQuery(id+"F2.wireOp",EDGE,"E27");var subQ1=sQuery(id+"F2.wireOp",EDGE,"E9");var subQ2=makeQuery(id+"F2.imprint","INTERSECT",VERTEX,{"disambiguationData":[OD(0.0)],"derivedFrom":[subQ1,subQ0]});Q22=makeQuery(id+"F2.imprint","IMPRINT",FACE,{"disambiguationData":[TD([[makeQuery(id+"F2.imprint","IMPRINT",EDGE,{"disambiguationData":[TD([[subQ2,-1.0]])],"derivedFrom":subQ1}),1.0]])]});}
            var Q23;
            {var subQ0=sQuery(id+"F2.wireOp",EDGE,"E27");var subQ1=sQuery(id+"F2.wireOp",EDGE,"E9");var subQ2=makeQuery(id+"F2.imprint","INTERSECT",VERTEX,{"disambiguationData":[OD(0.0)],"derivedFrom":[subQ1,subQ0]});Q23=makeQuery(id+"F2.imprint","IMPRINT",FACE,{"disambiguationData":[TD([[makeQuery(id+"F2.imprint","IMPRINT",EDGE,{"disambiguationData":[TD([[subQ2,-1.0]])],"derivedFrom":subQ1}),-1.0]])]});}
            var Q24;
            {var subQ0=sQuery(id+"F2.wireOp",EDGE,"E28");var subQ1=sQuery(id+"F2.wireOp",EDGE,"E10");var subQ2=makeQuery(id+"F2.imprint","INTERSECT",VERTEX,{"disambiguationData":[OD(0.0)],"derivedFrom":[subQ1,subQ0]});Q24=makeQuery(id+"F2.imprint","IMPRINT",FACE,{"disambiguationData":[TD([[makeQuery(id+"F2.imprint","IMPRINT",EDGE,{"disambiguationData":[TD([[subQ2,-1.0]])],"derivedFrom":subQ1}),1.0]])]});}
            var Q25;
            {var subQ0=sQuery(id+"F2.wireOp",EDGE,"E28");var subQ1=sQuery(id+"F2.wireOp",EDGE,"E10");var subQ2=makeQuery(id+"F2.imprint","INTERSECT",VERTEX,{"disambiguationData":[OD(0.0)],"derivedFrom":[subQ1,subQ0]});Q25=makeQuery(id+"F2.imprint","IMPRINT",FACE,{"disambiguationData":[TD([[makeQuery(id+"F2.imprint","IMPRINT",EDGE,{"disambiguationData":[TD([[subQ2,-1.0]])],"derivedFrom":subQ1}),-1.0]])]});}
            extrude(context, id + "F4", {"entities" : qUnion([Q0, Q1, Q2, Q3, Q4, Q5, Q6, Q7, Q8, Q9, Q10, Q11, Q12, Q13, Q14, Q15, Q16, Q17, Q18, Q19, Q20, Q21, Q22, Q23, Q24, Q25]), "operationType" : NewBodyOperationType.REMOVE, "oppositeDirection" : true, "depth" : 8 * mm, "offsetDistance" : 25 * mm});
        }
        {
            var Q0;
            Q0=makeQuery(id+"F0.imprint","IMPRINT",FACE,{"disambiguationData":[TD([[makeQuery(id+"F0.imprint","IMPRINT",EDGE,{"derivedFrom":sQuery(id+"F0.wireOp",EDGE,"E1.bottom")}),1.0]])]});
            extrude(context, id + "F5", {"entities" : qUnion([Q0]), "depth" : 10 * mm, "offsetDistance" : 25 * mm});
        }
        {
            var Q0;
            Q0=makeQuery(id+"F5.opExtrude","CAP_FACE",FACE,{"disambiguationData":[OSD([sQuery(id+"F0.wireOp",EDGE,"E1.bottom"),sQuery(id+"F0.wireOp",EDGE,"E1.top"),sQuery(id+"F0.wireOp",EDGE,"E1.left"),sQuery(id+"F0.wireOp",EDGE,"E1.right")])],"isStart":false});
            var sketch = newSketch(context, id + "F6", { "sketchPlane" : qUnion([Q0])});
            skCircle(sketch, "E29", {"center": v(-121.34, 2.28) * mm, "radius": 11 * mm});
            skCircle(sketch, "E30", {"center": v(-121.34, -8.72) * mm, "radius": 5 * mm});
            skSolve(sketch);
        }
        {
            var Q0;
            {var subQ0=sQuery(id+"F6.wireOp",EDGE,"E30");var subQ1=sQuery(id+"F6.wireOp",EDGE,"E29");var subQ2=makeQuery(id+"F6.imprint","INTERSECT",VERTEX,{"disambiguationData":[OD(0.0)],"derivedFrom":[subQ1,subQ0]});Q0=makeQuery(id+"F6.imprint","IMPRINT",FACE,{"disambiguationData":[TD([[makeQuery(id+"F6.imprint","IMPRINT",EDGE,{"disambiguationData":[TD([[subQ2,1.0]])],"derivedFrom":subQ1}),1.0]])]});}
            extrude(context, id + "F7", {"entities" : qUnion([Q0]), "operationType" : NewBodyOperationType.REMOVE, "oppositeDirection" : true, "depth" : 6 * mm, "offsetDistance" : 25 * mm});
        }
        {
            var Q0;
            {var subQ0=sQuery(id+"F6.wireOp",EDGE,"E30");var subQ1=sQuery(id+"F6.wireOp",EDGE,"E29");var subQ2=makeQuery(id+"F6.imprint","INTERSECT",VERTEX,{"disambiguationData":[OD(0.0)],"derivedFrom":[subQ1,subQ0]});Q0=makeQuery(id+"F6.imprint","IMPRINT",FACE,{"disambiguationData":[TD([[makeQuery(id+"F6.imprint","IMPRINT",EDGE,{"disambiguationData":[TD([[subQ2,-1.0]])],"derivedFrom":subQ1}),-1.0]])]});}
            var Q1;
            {var subQ0=sQuery(id+"F6.wireOp",EDGE,"E30");var subQ1=sQuery(id+"F6.wireOp",EDGE,"E29");var subQ2=makeQuery(id+"F6.imprint","INTERSECT",VERTEX,{"disambiguationData":[OD(0.0)],"derivedFrom":[subQ1,subQ0]});Q1=makeQuery(id+"F6.imprint","IMPRINT",FACE,{"disambiguationData":[TD([[makeQuery(id+"F6.imprint","IMPRINT",EDGE,{"disambiguationData":[TD([[subQ2,-1.0]])],"derivedFrom":subQ1}),1.0]])]});}
            extrude(context, id + "F8", {"entities" : qUnion([Q0, Q1]), "operationType" : NewBodyOperationType.REMOVE, "oppositeDirection" : true, "depth" : 8 * mm, "offsetDistance" : 25 * mm});
        }
    });
